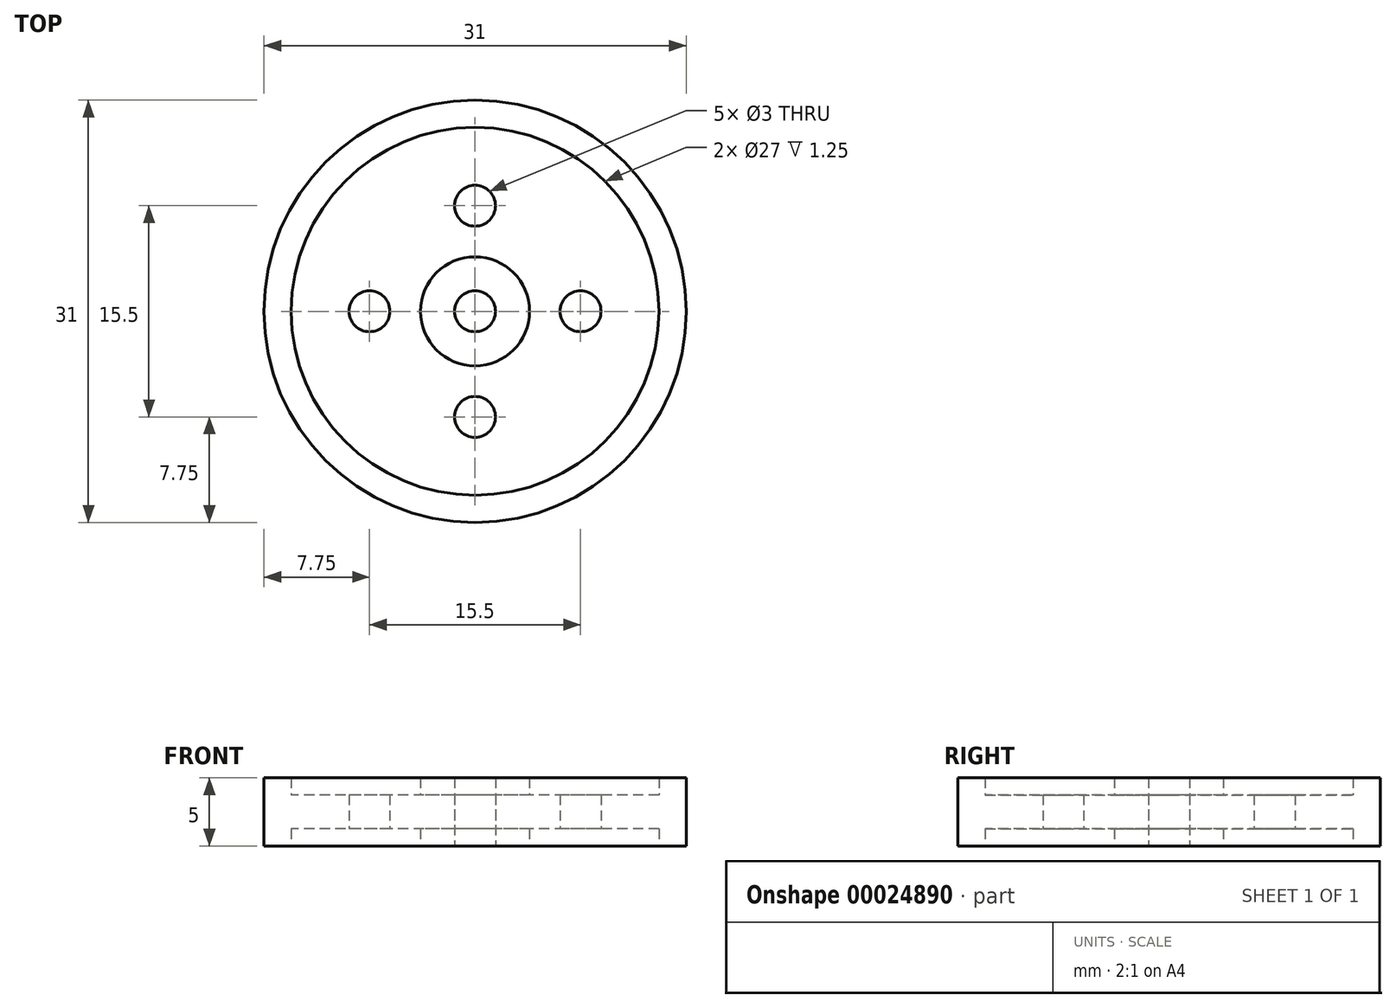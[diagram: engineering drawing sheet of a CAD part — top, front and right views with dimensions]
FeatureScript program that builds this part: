
annotation { "Feature Type Name" : "Feature", "Feature Type Description" : "" }
export const myFeature = defineFeature(function(context is Context, id is Id, definition is map)
    precondition{}
    {
        {
            var Q0;
            Q0=qCreatedBy(makeId("Top.planeOp"),FACE);
            var sketch = newSketch(context, id + "F0", { "sketchPlane" : qUnion([Q0])});
            skCircle(sketch, "E0", {"center": v(0, 0) * mm, "radius": 15.5 * mm});
            skCircle(sketch, "E1", {"center": v(0, 0) * mm, "radius": 1.5 * mm});
            skCircle(sketch, "E2", {"center": v(0, 0) * mm, "radius": 4 * mm});
            skCircle(sketch, "E3", {"center": v(0, 0) * mm, "radius": 13.5 * mm});
            skLineSegment(sketch, "E4", {"start": v(0, 0) * mm, "end": v(0, 15.5) * mm, "construction": true});
            skLineSegment(sketch, "E5", {"start": v(0, 15.5) * mm, "end": v(0, 0) * mm, "construction": true});
            skLineSegment(sketch, "E6", {"start": v(0, 0) * mm, "end": v(15.5, 0) * mm, "construction": true});
            skLineSegment(sketch, "E7", {"start": v(15.5, 0) * mm, "end": v(0, 0) * mm, "construction": true});
            skLineSegment(sketch, "E8", {"start": v(0, 0) * mm, "end": v(0, -15.5) * mm, "construction": true});
            skLineSegment(sketch, "E9", {"start": v(0, 0) * mm, "end": v(-15.5, 0) * mm, "construction": true});
            skPoint(sketch, "E10", {"position": v(0, 7.75) * mm});
            skCircle(sketch, "E11", {"center": v(0, 0) * mm, "radius": 7.75 * mm, "construction": true});
            skCircle(sketch, "E12", {"center": v(0, 7.75) * mm, "radius": 1.5 * mm});
            skCircle(sketch, "E13", {"center": v(7.75, 0) * mm, "radius": 1.5 * mm});
            skCircle(sketch, "E14", {"center": v(0, -7.75) * mm, "radius": 1.5 * mm});
            skCircle(sketch, "E15", {"center": v(-7.75, 0) * mm, "radius": 1.5 * mm});
            skSolve(sketch);
        }
        {
            var Q0;
            Q0=qSketchRegion(id+"F0",true);
            extrude(context, id + "F1", {"entities" : qUnion([Q0]), "depth" : 5 * mm});
        }
        {
            var Q0;
            Q0=makeQuery(id+"F0.imprint","IMPRINT",FACE,{"disambiguationData":[TD([[makeQuery(id+"F0.imprint","IMPRINT",EDGE,{"derivedFrom":sQuery(id+"F0.wireOp",EDGE,"E2")}),-1.0]])]});
            extrude(context, id + "F2", {"entities" : qUnion([Q0]), "operationType" : NewBodyOperationType.ADD, "depth" : 2.5 * mm + 1.25 * mm});
        }
        {
            var Q0;
            Q0=makeQuery(id+"F0.imprint","IMPRINT",FACE,{"disambiguationData":[TD([[makeQuery(id+"F0.imprint","IMPRINT",EDGE,{"derivedFrom":sQuery(id+"F0.wireOp",EDGE,"E2")}),-1.0]])]});
            extrude(context, id + "F3", {"entities" : qUnion([Q0]), "operationType" : NewBodyOperationType.REMOVE, "depth" : 1.25 * mm});
        }
        {
            var Q0;
            Q0=makeQuery(id+"F0.imprint","IMPRINT",FACE,{"disambiguationData":[TD([[makeQuery(id+"F0.imprint","IMPRINT",EDGE,{"derivedFrom":sQuery(id+"F0.wireOp",EDGE,"E1")}),-1.0]])]});
            extrude(context, id + "F4", {"entities" : qUnion([Q0]), "operationType" : NewBodyOperationType.ADD, "depth" : 5 * mm});
        }
    });
